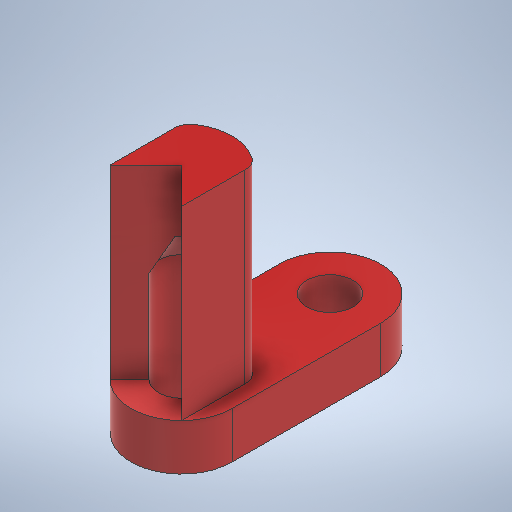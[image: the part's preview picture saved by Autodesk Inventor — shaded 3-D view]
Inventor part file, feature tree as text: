
AUTODESK INVENTOR PART (.ipt)
format: ipt  version: 2025.1 (Build 291241000, 241)  size: 326,656 bytes
history: native  units: in
note: dims shown in document units (in); Inventor stores cm internally (conversion verified against a paired STEP export)
features: extrude x5, sketch x5, projected_geometry x3, other x2, fillet x1, chamfer x1
ambient origin geometry x8: Origin, YZ Plane, XZ Plane, XY Plane, X Axis, Y Axis, Z Axis, Center Point
bodies: Solid1 (feature_tree)
feature tree (17):
  extrude  "Extrusion1"  Depth=0.1969in
  extrude  "Extrusion2"  TaperAngle=45.0deg  [1 undecoded]
  extrude  "Extrusion3"  Depth=0.1969in
  extrude  "Extrusion4"  Depth=0.1969in TaperAngle=0.0deg
  extrude  "Extrusion5"  Depth=0.3937in TaperAngle=0.0deg
  fillet  "Fillet1"  Radius=0.0787in
  chamfer  "Chamfer1"  Distance=0.0787in Angle=60.0deg
  sketch  "Sketch1"  dims[d0=0.4291in d1=0.6299in d2=0.4331in d3=0.1969in d4=0.1969in d5=0.1969in d6=0.0in d7=0.1969in]
  sketch  "Sketch2"  dims[d8=0.1969in d9=45.0deg]
  projected_geometry  "Projected Loop1"
  projected_geometry  "Projected Loop2"
  sketch  "Sketch3"  dims[d10=0.7874in d11=0.0in d12=0.1969in]
  projected_geometry  "Projected Loop3"
  sketch  "Sketch4"  dims[d13=0.1969in d14=0.1575in d15=0.0in]
  sketch  "Sketch5"  dims[d16=0.5251in d17=0.0in d18=0.3937in d19=0.0in d20=0.0787in d21=0.0787in d22=0.0787in d23=60.0deg]
  other  "Finish1"
  other  "Finish2"
note: 1 required parameter value undecoded (feature->parameter linkage not recoverable at this tier; creation-order binding heuristic only, values carry confidence <= 0.55)
